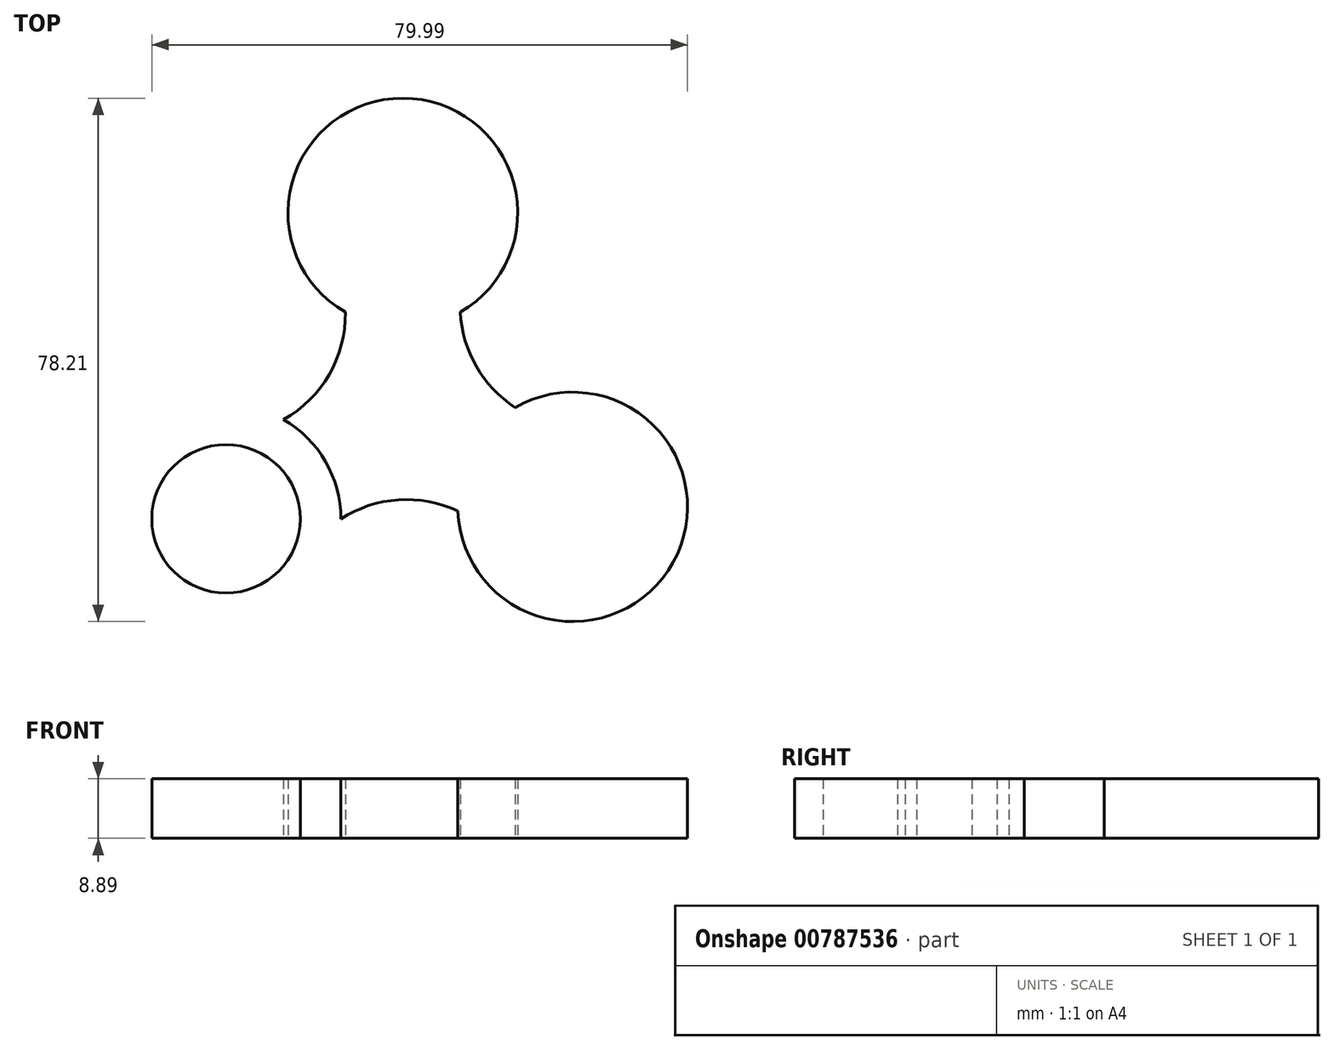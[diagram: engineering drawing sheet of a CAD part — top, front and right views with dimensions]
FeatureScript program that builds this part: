
annotation { "Feature Type Name" : "Feature", "Feature Type Description" : "" }
export const myFeature = defineFeature(function(context is Context, id is Id, definition is map)
    precondition{}
    {
        {
            var Q0;
            Q0=qCreatedBy(makeId("Top.planeOp"),FACE);
            var sketch = newSketch(context, id + "F0", { "sketchPlane" : qUnion([Q0])});
            skCircle(sketch, "E0", {"center": v(0, 0) * mm, "radius": 11.09 * mm});
            skCircle(sketch, "E1", {"center": v(0, 30.48) * mm, "radius": 11.09 * mm});
            skCircle(sketch, "E2", {"center": v(25.36, -13.45) * mm, "radius": 11.09 * mm});
            skCircle(sketch, "E3", {"center": v(-26.4, -15.24) * mm, "radius": 11.09 * mm});
            skCircle(sketch, "E4", {"center": v(-26.4, -15.24) * mm, "radius": 17.15 * mm});
            skCircle(sketch, "E5", {"center": v(25.36, -13.45) * mm, "radius": 17.15 * mm});
            skCircle(sketch, "E6", {"center": v(0, 30.48) * mm, "radius": 17.15 * mm});
            skArc(sketch, "E7", {"start": v(-17.82, -0.4) * mm, "mid": v(-11, 6.35) * mm, "end": v(-8.57, 15.63) * mm});
            skArc(sketch, "E8", {"start": v(8.57, 15.63) * mm, "mid": v(10.97, 7.53) * mm, "end": v(16.8, 1.4) * mm});
            skArc(sketch, "E9", {"start": v(8.23, -14.07) * mm, "mid": v(-0.66, -12.4) * mm, "end": v(-9.25, -15.24) * mm});
            skSolve(sketch);
        }
        {
            var Q0;
            {var subQ0=sQuery(id+"F0.wireOp",EDGE,"FYFptZ7j-349R-miWC-azGU-p6po9625XQA6");var subQ1=sQuery(id+"F0.wireOp",EDGE,"E1");var subQ2=makeQuery(id+"F0.imprint","INTERSECT",VERTEX,{"derivedFrom":[subQ1,subQ0]});Q0=makeQuery(id+"F0.imprint","IMPRINT",FACE,{"disambiguationData":[TD([[makeQuery(id+"F0.imprint","IMPRINT",EDGE,{"disambiguationData":[TD([[subQ2,1.0]])],"derivedFrom":subQ1}),1.0]])]});}
            var Q1;
            {var subQ0=sQuery(id+"F0.wireOp",EDGE,"FYFptZ7j-349R-miWC-azGU-p6po9625XQA6");var subQ1=sQuery(id+"F0.wireOp",EDGE,"E1");var subQ2=makeQuery(id+"F0.imprint","INTERSECT",VERTEX,{"derivedFrom":[subQ1,subQ0]});Q1=makeQuery(id+"F0.imprint","IMPRINT",FACE,{"disambiguationData":[TD([[makeQuery(id+"F0.imprint","IMPRINT",EDGE,{"disambiguationData":[TD([[subQ2,-1.0]])],"derivedFrom":subQ1}),1.0]])]});}
            var Q2;
            {var subQ0=sQuery(id+"F0.wireOp",EDGE,"HJxREoaR-VNGx-fY1l-on0U-KYuJbwK9EL4g");var subQ1=sQuery(id+"F0.wireOp",EDGE,"E2");var subQ2=makeQuery(id+"F0.imprint","INTERSECT",VERTEX,{"derivedFrom":[subQ1,subQ0]});Q2=makeQuery(id+"F0.imprint","IMPRINT",FACE,{"disambiguationData":[TD([[makeQuery(id+"F0.imprint","IMPRINT",EDGE,{"disambiguationData":[TD([[subQ2,-1.0]])],"derivedFrom":subQ1}),-1.0]])]});}
            var Q3;
            {var subQ0=sQuery(id+"F0.wireOp",EDGE,"FYFptZ7j-349R-miWC-azGU-p6po9625XQA6");var subQ1=sQuery(id+"F0.wireOp",EDGE,"E1");var subQ2=makeQuery(id+"F0.imprint","INTERSECT",VERTEX,{"derivedFrom":[subQ1,subQ0]});Q3=makeQuery(id+"F0.imprint","IMPRINT",FACE,{"disambiguationData":[TD([[makeQuery(id+"F0.imprint","IMPRINT",EDGE,{"disambiguationData":[TD([[subQ2,1.0]])],"derivedFrom":subQ1}),-1.0]])]});}
            var Q4;
            {var subQ0=sQuery(id+"F0.wireOp",EDGE,"HJxREoaR-VNGx-fY1l-on0U-KYuJbwK9EL4g");var subQ1=sQuery(id+"F0.wireOp",EDGE,"E2");var subQ2=makeQuery(id+"F0.imprint","INTERSECT",VERTEX,{"derivedFrom":[subQ1,subQ0]});Q4=makeQuery(id+"F0.imprint","IMPRINT",FACE,{"disambiguationData":[TD([[makeQuery(id+"F0.imprint","IMPRINT",EDGE,{"disambiguationData":[TD([[subQ2,-1.0]])],"derivedFrom":subQ1}),1.0]])]});}
            var Q5;
            {var subQ0=sQuery(id+"F0.wireOp",EDGE,"W4YPu0gR-WOF5-0gse-jw3N-QmrCXtD0cmDF");var subQ1=sQuery(id+"F0.wireOp",EDGE,"E3");var subQ2=makeQuery(id+"F0.imprint","INTERSECT",VERTEX,{"derivedFrom":[subQ1,subQ0]});Q5=makeQuery(id+"F0.imprint","IMPRINT",FACE,{"disambiguationData":[TD([[makeQuery(id+"F0.imprint","IMPRINT",EDGE,{"disambiguationData":[TD([[subQ2,-1.0]])],"derivedFrom":subQ1}),1.0]])]});}
            var Q6;
            {var subQ0=sQuery(id+"F0.wireOp",EDGE,"W4YPu0gR-WOF5-0gse-jw3N-QmrCXtD0cmDF");var subQ1=sQuery(id+"F0.wireOp",EDGE,"E3");var subQ2=makeQuery(id+"F0.imprint","INTERSECT",VERTEX,{"derivedFrom":[subQ1,subQ0]});Q6=makeQuery(id+"F0.imprint","IMPRINT",FACE,{"disambiguationData":[TD([[makeQuery(id+"F0.imprint","IMPRINT",EDGE,{"disambiguationData":[TD([[subQ2,1.0]])],"derivedFrom":subQ1}),1.0]])]});}
            var Q7;
            {var subQ3=sQuery(id+"F0.wireOp",EDGE,"FYFptZ7j-349R-miWC-azGU-p6po9625XQA6");var subQ7=sQuery(id+"F0.wireOp",EDGE,"E1");var subQ8=makeQuery(id+"F0.imprint","INTERSECT",VERTEX,{"derivedFrom":[subQ7,subQ3]});Q7=makeQuery(id+"F0.imprint","IMPRINT",FACE,{"disambiguationData":[TD([[makeQuery(id+"F0.imprint","IMPRINT",EDGE,{"disambiguationData":[TD([[subQ8,-1.0]])],"derivedFrom":subQ7}),-1.0]])]});}
            var Q8;
            {var subQ2=sQuery(id+"F0.wireOp",EDGE,"HJxREoaR-VNGx-fY1l-on0U-KYuJbwK9EL4g");var subQ7=sQuery(id+"F0.wireOp",EDGE,"E2");var subQ8=makeQuery(id+"F0.imprint","INTERSECT",VERTEX,{"derivedFrom":[subQ7,subQ2]});Q8=makeQuery(id+"F0.imprint","IMPRINT",FACE,{"disambiguationData":[TD([[makeQuery(id+"F0.imprint","IMPRINT",EDGE,{"disambiguationData":[TD([[subQ8,1.0]])],"derivedFrom":subQ7}),-1.0]])]});}
            var Q9;
            {var subQ0=sQuery(id+"F0.wireOp",EDGE,"E4");var subQ2=makeQuery(id+"F0.imprint","IMPRINT",VERTEX,{"derivedFrom":subQ0});Q9=makeQuery(id+"F0.imprint","IMPRINT",FACE,{"disambiguationData":[TD([[makeQuery(id+"F0.imprint","IMPRINT",EDGE,{"disambiguationData":[TD([[subQ2,1.0]])],"derivedFrom":subQ0}),1.0]])]});}
            var Q10;
            {var subQ0=sQuery(id+"F0.wireOp",EDGE,"HJxREoaR-VNGx-fY1l-on0U-KYuJbwK9EL4g");var subQ1=sQuery(id+"F0.wireOp",EDGE,"E2");var subQ2=makeQuery(id+"F0.imprint","INTERSECT",VERTEX,{"derivedFrom":[subQ1,subQ0]});Q10=makeQuery(id+"F0.imprint","IMPRINT",FACE,{"disambiguationData":[TD([[makeQuery(id+"F0.imprint","IMPRINT",EDGE,{"disambiguationData":[TD([[subQ2,1.0]])],"derivedFrom":subQ1}),1.0]])]});}
            var Q11;
            Q11=makeQuery(id+"F0.imprint","IMPRINT",FACE,{"disambiguationData":[TD([[makeQuery(id+"F0.imprint","IMPRINT",EDGE,{"derivedFrom":sQuery(id+"F0.wireOp",EDGE,"E0")}),-1.0]])]});
            var Q12;
            Q12=makeQuery(id+"F0.imprint","IMPRINT",FACE,{"disambiguationData":[TD([[makeQuery(id+"F0.imprint","IMPRINT",EDGE,{"derivedFrom":sQuery(id+"F0.wireOp",EDGE,"E0")}),1.0]])]});
            extrude(context, id + "F1", {"entities" : qUnion([Q0, Q1, Q2, Q3, Q4, Q5, Q6, Q7, Q8, Q9, Q10, Q11, Q12]), "depth" : 8.9 * mm, "offsetDistance" : 25.4 * mm});
        }
    });
